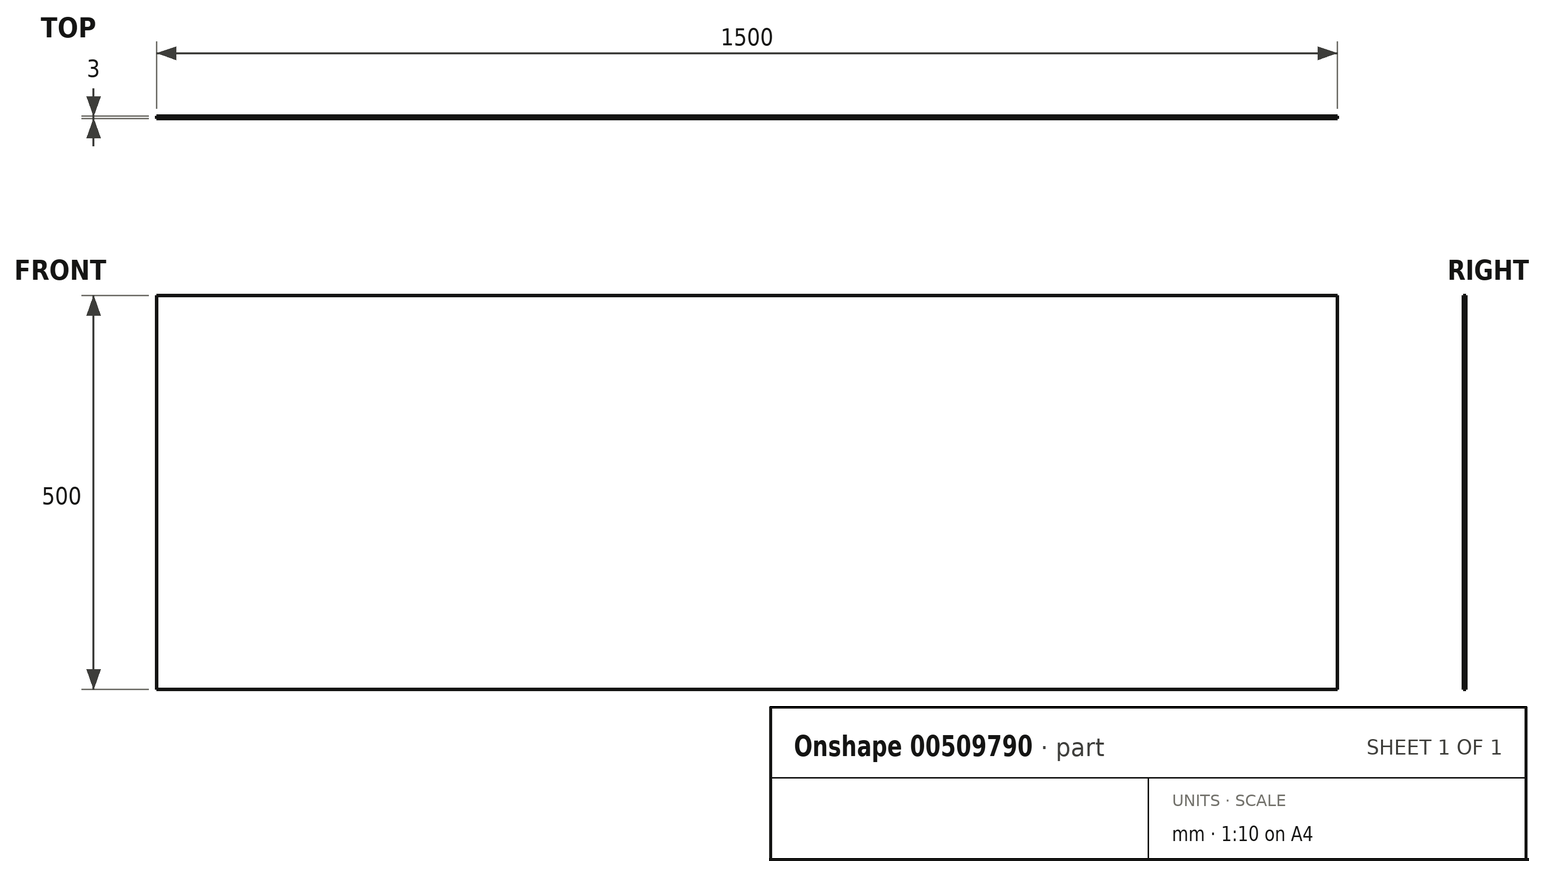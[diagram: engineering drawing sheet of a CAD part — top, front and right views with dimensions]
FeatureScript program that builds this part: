
annotation { "Feature Type Name" : "Feature", "Feature Type Description" : "" }
export const myFeature = defineFeature(function(context is Context, id is Id, definition is map)
    precondition{}
    {
        {
            var Q0;
            Q0=qCreatedBy(makeId("Front.planeOp"),FACE);
            var sketch = newSketch(context, id + "F0", { "sketchPlane" : qUnion([Q0])});
            skLineSegment(sketch, "E0.bottom", {"start": v(750, -250) * mm, "end": v(-750, -250) * mm});
            skLineSegment(sketch, "E0.top", {"start": v(750, 250) * mm, "end": v(-750, 250) * mm});
            skLineSegment(sketch, "E0.left", {"start": v(750, -250) * mm, "end": v(750, 250) * mm});
            skLineSegment(sketch, "E0.right", {"start": v(-750, -250) * mm, "end": v(-750, 250) * mm});
            skPoint(sketch, "E0.middle", {"position": v(0, 0) * mm});
            skSolve(sketch);
        }
        {
            var Q0;
            Q0 = qSketchRegion(id + "F0", true);
            extrude(context, id + "F1", {"entities" : qUnion([Q0]), "depth" : 3 * mm});
        }
    });
